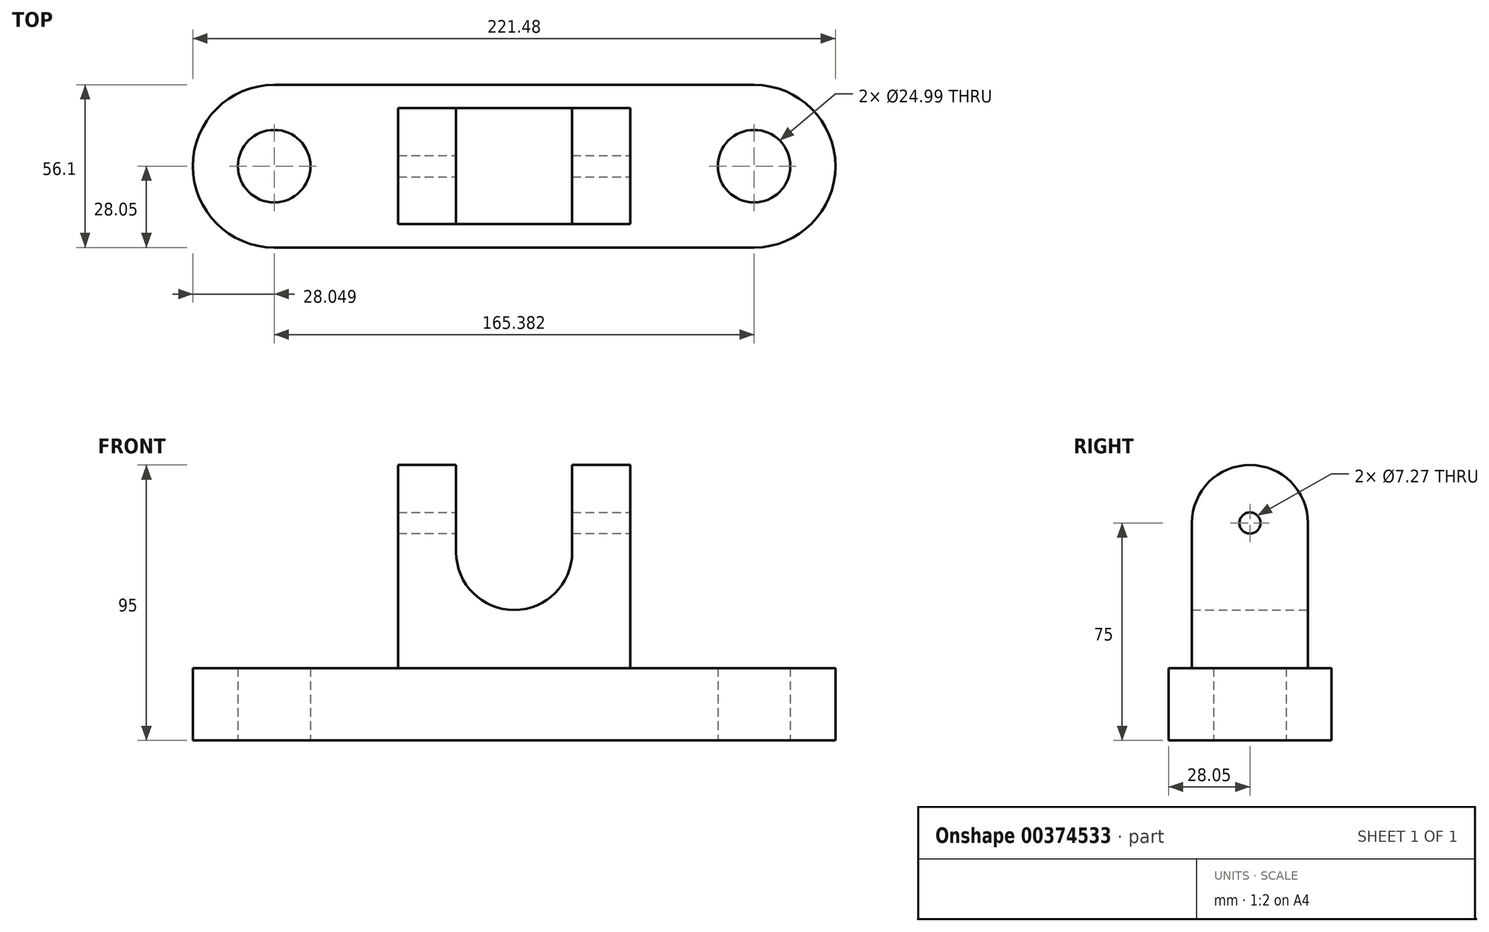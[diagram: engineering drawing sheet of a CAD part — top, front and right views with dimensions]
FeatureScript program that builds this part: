
annotation { "Feature Type Name" : "Feature", "Feature Type Description" : "" }
export const myFeature = defineFeature(function(context is Context, id is Id, definition is map)
    precondition{}
    {
        {
            var Q0;
            Q0=qCreatedBy(makeId("Top.planeOp"),FACE);
            var sketch = newSketch(context, id + "F0", { "sketchPlane" : qUnion([Q0])});
            skLineSegment(sketch, "E0.bottom", {"start": v(82.7, -28.05) * mm, "end": v(-82.7, -28.05) * mm});
            skLineSegment(sketch, "E0.top", {"start": v(82.7, 28.05) * mm, "end": v(-82.7, 28.05) * mm});
            skPoint(sketch, "E0.middle", {"position": v(0, 0) * mm});
            skArc(sketch, "E1", {"start": v(82.7, -28.05) * mm, "mid": v(110.74, 0) * mm, "end": v(82.7, 28.05) * mm});
            skArc(sketch, "E2", {"start": v(-82.7, 28.05) * mm, "mid": v(-110.74, 0) * mm, "end": v(-82.7, -28.05) * mm});
            skCircle(sketch, "E3", {"center": v(-82.7, 0) * mm, "radius": 12.5 * mm});
            skCircle(sketch, "E4", {"center": v(82.7, 0) * mm, "radius": 12.5 * mm});
            skSolve(sketch);
        }
        {
            var Q0;
            Q0=makeQuery(id+"F0.imprint","IMPRINT",FACE,{"disambiguationData":[TD([[makeQuery(id+"F0.imprint","IMPRINT",EDGE,{"derivedFrom":sQuery(id+"F0.wireOp",EDGE,"E0.bottom")}),-1.0]])]});
            extrude(context, id + "F1", {"entities" : qUnion([Q0]), "depth" : 25 * mm});
        }
        {
            var Q0;
            Q0=qCreatedBy(makeId("Front.planeOp"),FACE);
            var sketch = newSketch(context, id + "F2", { "sketchPlane" : qUnion([Q0])});
            skLineSegment(sketch, "E5.0", {"start": v(40, 25) * mm, "end": v(-40, 25) * mm});
            skLineSegment(sketch, "E6", {"start": v(-40, 25) * mm, "end": v(-40, 95) * mm});
            skLineSegment(sketch, "E7", {"start": v(-40, 95) * mm, "end": v(-20, 95) * mm});
            skLineSegment(sketch, "E8", {"start": v(-20, 95) * mm, "end": v(-20, 45) * mm});
            skLineSegment(sketch, "E9", {"start": v(-20, 45) * mm, "end": v(20, 45) * mm});
            skLineSegment(sketch, "E10", {"start": v(20, 45) * mm, "end": v(20, 95) * mm});
            skLineSegment(sketch, "E11", {"start": v(20, 95) * mm, "end": v(40, 95) * mm});
            skLineSegment(sketch, "E12", {"start": v(40, 95) * mm, "end": v(40, 25) * mm});
            skPoint(sketch, "E13.orphan", {"position": v(-82.7, 25) * mm});
            skPoint(sketch, "E14.orphan", {"position": v(82.7, 25) * mm});
            skSolve(sketch);
        }
        {
            var Q0;
            Q0=makeQuery(id+"F2.imprint","IMPRINT",FACE,{"disambiguationData":[TD([[makeQuery(id+"F2.imprint","IMPRINT",EDGE,{"derivedFrom":sQuery(id+"F2.wireOp",EDGE,"E5.0")}),-1.0]])]});
            extrude(context, id + "F3", {"entities" : qUnion([Q0]), "operationType" : NewBodyOperationType.ADD, "endBound" : BoundingType.SYMMETRIC, "oppositeDirection" : true, "depth" : 40 * mm});
        }
        {
            var Q0;
            Q0=makeQuery(id+"F3.opExtrude","SWEPT_EDGE",EDGE,{"disambiguationData":[OSD([sQuery(id+"F2.wireOp",EDGE,"E8"),sQuery(id+"F2.wireOp",EDGE,"E9")])]});
            var Q1;
            Q1=makeQuery(id+"F3.opExtrude","SWEPT_EDGE",EDGE,{"disambiguationData":[OSD([sQuery(id+"F2.wireOp",EDGE,"E9"),sQuery(id+"F2.wireOp",EDGE,"E10")])]});
            fillet(context, id + "F4", {"entities" : qUnion([Q0, Q1]), "radius" : 20 * mm, "tangentPropagation" : true, "allowEdgeOverflow" : false});
        }
        {
            var Q0;
            Q0=makeQuery(id+"F3.opExtrude","CAP_EDGE",EDGE,{"disambiguationData":[OSD([sQuery(id+"F2.wireOp",EDGE,"E7")])],"isStart":true});
            var Q1;
            Q1=makeQuery(id+"F3.opExtrude","CAP_EDGE",EDGE,{"disambiguationData":[OSD([sQuery(id+"F2.wireOp",EDGE,"E7")])],"isStart":false});
            var Q2;
            Q2=makeQuery(id+"F3.opExtrude","CAP_EDGE",EDGE,{"disambiguationData":[OSD([sQuery(id+"F2.wireOp",EDGE,"E11")])],"isStart":true});
            var Q3;
            Q3=makeQuery(id+"F3.opExtrude","CAP_EDGE",EDGE,{"disambiguationData":[OSD([sQuery(id+"F2.wireOp",EDGE,"E11")])],"isStart":false});
            fillet(context, id + "F5", {"entities" : qUnion([Q0, Q1, Q2, Q3]), "radius" : 20 * mm, "tangentPropagation" : true, "allowEdgeOverflow" : false});
        }
        {
            var Q0;
            Q0=makeQuery(id+"F3.opExtrude","SWEPT_FACE",FACE,{"disambiguationData":[OSD([sQuery(id+"F2.wireOp",EDGE,"E12")])]});
            var sketch = newSketch(context, id + "F6", { "sketchPlane" : qUnion([Q0])});
            skCircle(sketch, "E15", {"center": v(0, 75) * mm, "radius": 3.64 * mm});
            skSolve(sketch);
        }
        {
            var Q0;
            Q0=makeQuery(id+"F6.imprint","IMPRINT",FACE,{"disambiguationData":[TD([[makeQuery(id+"F6.imprint","IMPRINT",EDGE,{"derivedFrom":sQuery(id+"F6.wireOp",EDGE,"E15")}),1.0]])]});
            extrude(context, id + "F7", {"entities" : qUnion([Q0]), "operationType" : NewBodyOperationType.REMOVE, "endBound" : BoundingType.THROUGH_ALL, "oppositeDirection" : true, "depth" : 25 * mm});
        }
    });
